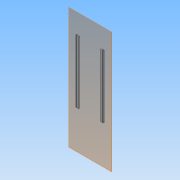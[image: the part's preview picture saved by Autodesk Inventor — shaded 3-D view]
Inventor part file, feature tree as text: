
AUTODESK INVENTOR PART (.ipt)
format: ipt  version: 2013 (Build 170138000, 138)  size: 122,880 bytes
history: native  units: in
note: dims shown in document units (in); Inventor stores cm internally (conversion verified against a paired STEP export)
features: extrude x2, sketch x2, reference x2, plane x1, projected_geometry x1
ambient origin geometry x8: Origin, YZ Plane, XZ Plane, XY Plane, X Axis, Y Axis, Z Axis, Center Point
bodies: Solid1 (feature_tree)
feature tree (8):
  plane  "Work Plane1"
  extrude  "Extrusion1"  Depth=0.75in TaperAngle=0.0deg
  extrude  "Extrusion2"  Depth=0.5in
  sketch  "Sketch1"  dims[d1=2.5in d2=0.75in d3=0.0in]
  reference  "Reference1"
  reference  "Reference2"
  sketch  "Sketch2"  dims[d5=0.48in d6=0.5in d7=0.5in d8=0.5in d9=0.0in]
  projected_geometry  "Projected Loop1"
